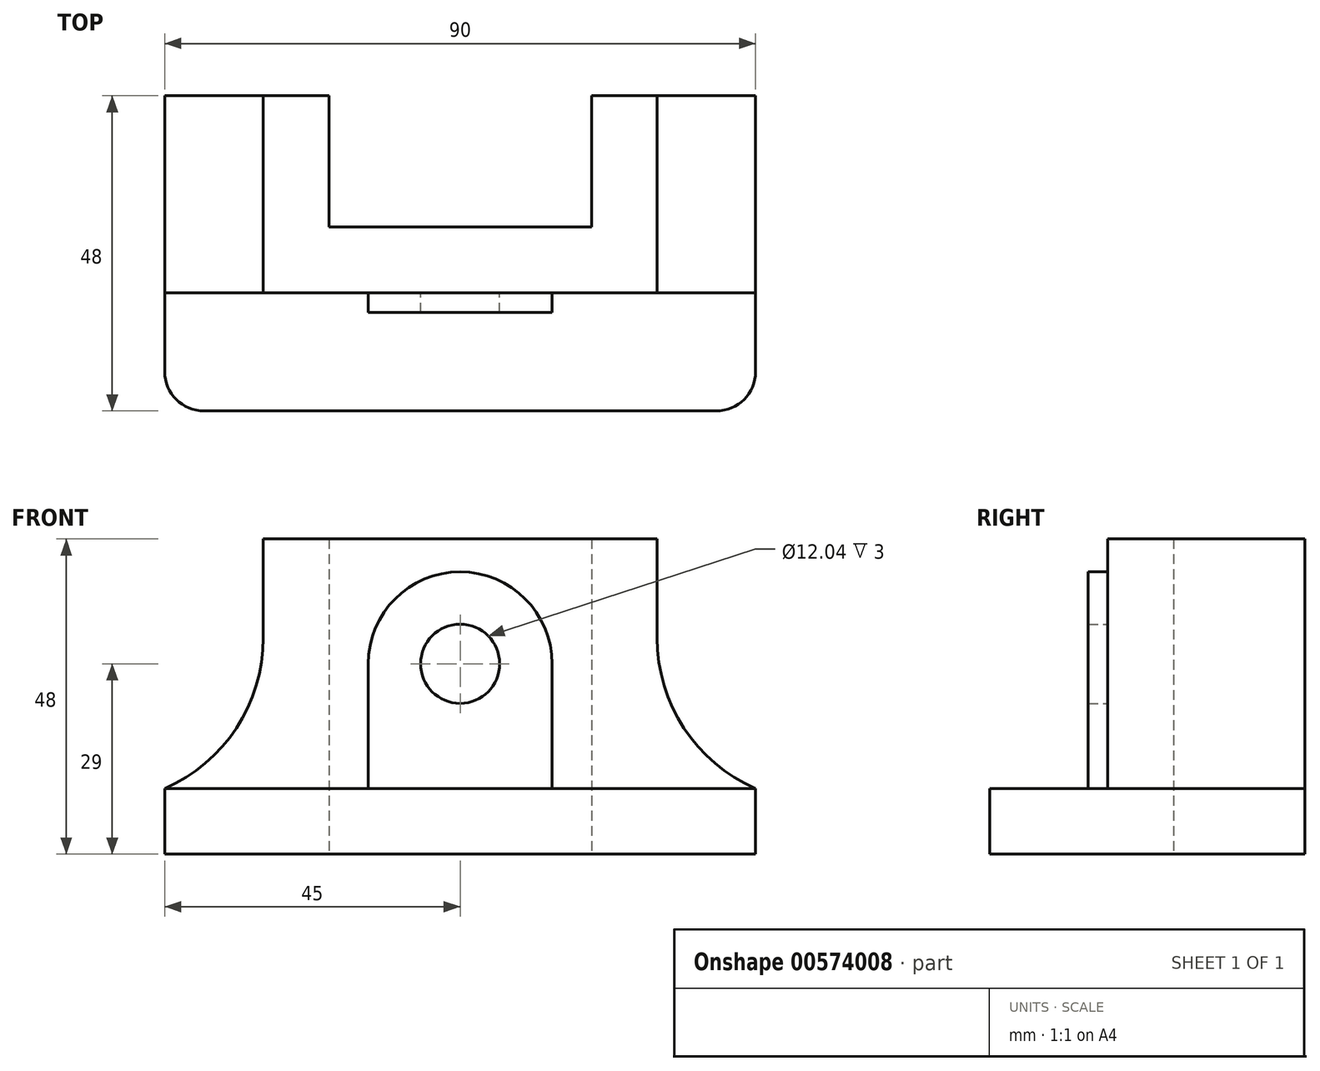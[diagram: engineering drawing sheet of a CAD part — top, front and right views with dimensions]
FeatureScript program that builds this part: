
annotation { "Feature Type Name" : "Feature", "Feature Type Description" : "" }
export const myFeature = defineFeature(function(context is Context, id is Id, definition is map)
    precondition{}
    {
        {
            var Q0;
            Q0=qCreatedBy(makeId("Top.planeOp"),FACE);
            var sketch = newSketch(context, id + "F0", { "sketchPlane" : qUnion([Q0])});
            skLineSegment(sketch, "E0", {"start": v(0, 10) * mm, "end": v(-20, 10) * mm});
            skLineSegment(sketch, "E1", {"start": v(-20, 10) * mm, "end": v(-20, 30) * mm});
            skLineSegment(sketch, "E2", {"start": v(-20, 30) * mm, "end": v(-30, 30) * mm});
            skLineSegment(sketch, "E3", {"start": v(-30, 30) * mm, "end": v(-30, 0) * mm});
            skLineSegment(sketch, "E4", {"start": v(-30, 0) * mm, "end": v(0, 0) * mm});
            skLineSegment(sketch, "E5", {"start": v(-30, 30) * mm, "end": v(-45, 30) * mm});
            skLineSegment(sketch, "E6", {"start": v(-45, 30) * mm, "end": v(-45, -18) * mm});
            skLineSegment(sketch, "E7", {"start": v(-45, -18) * mm, "end": v(0, -18) * mm});
            skLineSegment(sketch, "E8.MirrorCS", {"start": v(0, 10) * mm, "end": v(20, 10) * mm});
            skLineSegment(sketch, "E9.MirrorCS", {"start": v(20, 10) * mm, "end": v(20, 30) * mm});
            skLineSegment(sketch, "E10.MirrorCS", {"start": v(45, -18) * mm, "end": v(0, -18) * mm});
            skLineSegment(sketch, "E11.MirrorCS", {"start": v(45, 30) * mm, "end": v(45, -18) * mm});
            skLineSegment(sketch, "E12.MirrorCS", {"start": v(30, 30) * mm, "end": v(45, 30) * mm});
            skLineSegment(sketch, "E13.MirrorCS", {"start": v(30, 0) * mm, "end": v(0, 0) * mm});
            skLineSegment(sketch, "E14.MirrorCS", {"start": v(20, 30) * mm, "end": v(30, 30) * mm});
            skLineSegment(sketch, "E15.MirrorCS", {"start": v(30, 30) * mm, "end": v(30, 0) * mm});
            skSolve(sketch);
        }
        {
            var Q0;
            Q0=makeQuery(id+"F0.imprint","IMPRINT",FACE,{"disambiguationData":[TD([[makeQuery(id+"F0.imprint","IMPRINT",EDGE,{"derivedFrom":sQuery(id+"F0.wireOp",EDGE,"E0")}),1.0]])]});
            extrude(context, id + "F1", {"entities" : qUnion([Q0]), "depth" : 48 * mm, "offsetDistance" : 25 * mm});
        }
        {
            var Q0;
            Q0 = qSketchRegion(id + "F0", true);
            extrude(context, id + "F2", {"entities" : qUnion([Q0]), "operationType" : NewBodyOperationType.ADD, "depth" : 10 * mm, "offsetDistance" : 25 * mm});
        }
        {
            var Q0;
            Q0=qCreatedBy(makeId("Front.planeOp"),FACE);
            var sketch = newSketch(context, id + "F3", { "sketchPlane" : qUnion([Q0])});
            skCircle(sketch, "E16", {"center": v(0, 29) * mm, "radius": 6.02 * mm});
            skArc(sketch, "E17", {"start": v(14, 29) * mm, "mid": v(0, 43) * mm, "end": v(-14, 29) * mm});
            skLineSegment(sketch, "E18", {"start": v(-14, 29) * mm, "end": v(-14, 10) * mm});
            skLineSegment(sketch, "E19", {"start": v(-14, 10) * mm, "end": v(14, 10) * mm});
            skLineSegment(sketch, "E20", {"start": v(14, 10) * mm, "end": v(14, 29) * mm});
            skSolve(sketch);
        }
        {
            var Q0;
            Q0=makeQuery(id+"F3.imprint","IMPRINT",FACE,{"disambiguationData":[TD([[makeQuery(id+"F3.imprint","IMPRINT",EDGE,{"derivedFrom":sQuery(id+"F3.wireOp",EDGE,"E16")}),-1.0]])]});
            extrude(context, id + "F4", {"entities" : qUnion([Q0]), "operationType" : NewBodyOperationType.ADD, "depth" : 3 * mm, "offsetDistance" : 25 * mm});
        }
        {
            var Q0;
            Q0=makeQuery(id+"F2.boolean.opBoolean","INTERSECT",EDGE,{"derivedFrom":[makeQuery(id+"F1.opExtrude","SWEPT_FACE",FACE,{"disambiguationData":[OSD([sQuery(id+"F0.wireOp",EDGE,"E15.MirrorCS")])]}),makeQuery(id+"F2.opExtrude","CAP_FACE",FACE,{"disambiguationData":[OSD([sQuery(id+"F0.wireOp",EDGE,"E0"),sQuery(id+"F0.wireOp",EDGE,"E1"),sQuery(id+"F0.wireOp",EDGE,"E2"),sQuery(id+"F0.wireOp",EDGE,"E5"),sQuery(id+"F0.wireOp",EDGE,"E6"),sQuery(id+"F0.wireOp",EDGE,"E7"),sQuery(id+"F0.wireOp",EDGE,"E8.MirrorCS"),sQuery(id+"F0.wireOp",EDGE,"E9.MirrorCS"),sQuery(id+"F0.wireOp",EDGE,"E10.MirrorCS"),sQuery(id+"F0.wireOp",EDGE,"E11.MirrorCS"),sQuery(id+"F0.wireOp",EDGE,"E12.MirrorCS"),sQuery(id+"F0.wireOp",EDGE,"E14.MirrorCS")])],"isStart":false})]});
            var Q1;
            Q1=makeQuery(id+"F2.boolean.opBoolean","INTERSECT",EDGE,{"derivedFrom":[makeQuery(id+"F1.opExtrude","SWEPT_FACE",FACE,{"disambiguationData":[OSD([sQuery(id+"F0.wireOp",EDGE,"E3")])]}),makeQuery(id+"F2.opExtrude","CAP_FACE",FACE,{"disambiguationData":[OSD([sQuery(id+"F0.wireOp",EDGE,"E0"),sQuery(id+"F0.wireOp",EDGE,"E1"),sQuery(id+"F0.wireOp",EDGE,"E2"),sQuery(id+"F0.wireOp",EDGE,"E5"),sQuery(id+"F0.wireOp",EDGE,"E6"),sQuery(id+"F0.wireOp",EDGE,"E7"),sQuery(id+"F0.wireOp",EDGE,"E8.MirrorCS"),sQuery(id+"F0.wireOp",EDGE,"E9.MirrorCS"),sQuery(id+"F0.wireOp",EDGE,"E10.MirrorCS"),sQuery(id+"F0.wireOp",EDGE,"E11.MirrorCS"),sQuery(id+"F0.wireOp",EDGE,"E12.MirrorCS"),sQuery(id+"F0.wireOp",EDGE,"E14.MirrorCS")])],"isStart":false})]});
            fillet(context, id + "F5", {"entities" : qUnion([Q0, Q1]), "radius" : 25 * mm, "tangentPropagation" : true, "allowEdgeOverflow" : false});
        }
        {
            var Q0;
            Q0=makeQuery(id+"F2.opExtrude","SWEPT_EDGE",EDGE,{"disambiguationData":[OSD([sQuery(id+"F0.wireOp",EDGE,"E6"),sQuery(id+"F0.wireOp",EDGE,"E7")])]});
            var Q1;
            Q1=makeQuery(id+"F2.opExtrude","SWEPT_EDGE",EDGE,{"disambiguationData":[OSD([sQuery(id+"F0.wireOp",EDGE,"E10.MirrorCS"),sQuery(id+"F0.wireOp",EDGE,"E11.MirrorCS")])]});
            fillet(context, id + "F6", {"entities" : qUnion([Q0, Q1]), "radius" : 6 * mm, "tangentPropagation" : true, "allowEdgeOverflow" : false});
        }
    });
